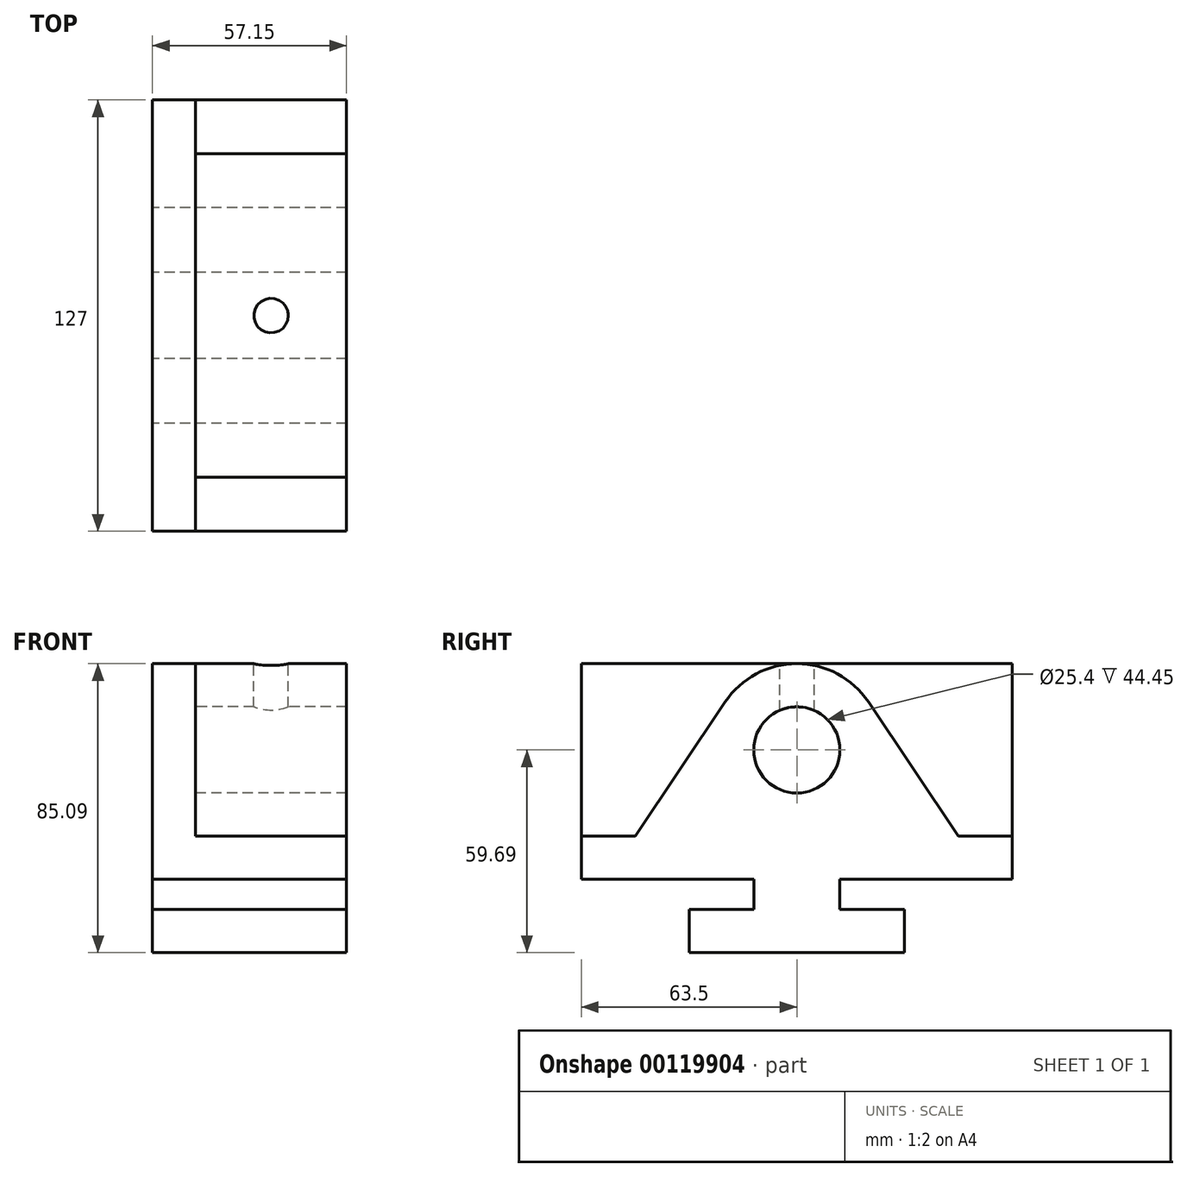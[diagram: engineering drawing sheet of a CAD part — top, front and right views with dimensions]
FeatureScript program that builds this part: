
annotation { "Feature Type Name" : "Feature", "Feature Type Description" : "" }
export const myFeature = defineFeature(function(context is Context, id is Id, definition is map)
    precondition{}
    {
        {
            var Q0;
            Q0=qCreatedBy(makeId("Right.planeOp"),FACE);
            var sketch = newSketch(context, id + "F0", { "sketchPlane" : qUnion([Q0])});
            skLineSegment(sketch, "E0", {"start": v(0, 0) * mm, "end": v(-31.75, 0) * mm});
            skLineSegment(sketch, "E1", {"start": v(-31.75, 0) * mm, "end": v(-31.75, 12.7) * mm});
            skLineSegment(sketch, "E2", {"start": v(-31.75, 12.7) * mm, "end": v(-12.7, 12.7) * mm});
            skLineSegment(sketch, "E3", {"start": v(-12.7, 12.7) * mm, "end": v(-12.7, 21.59) * mm});
            skLineSegment(sketch, "E4", {"start": v(-12.7, 21.59) * mm, "end": v(-63.5, 21.59) * mm});
            skLineSegment(sketch, "E5", {"start": v(-63.5, 21.6) * mm, "end": v(-63.5, 85.1) * mm});
            skLineSegment(sketch, "E6", {"start": v(0, 0) * mm, "end": v(0, 85.09) * mm, "construction": true});
            skLineSegment(sketch, "E7", {"start": v(0, 85.1) * mm, "end": v(-63.5, 85.1) * mm});
            skLineSegment(sketch, "E8.MirrorCS", {"start": v(31.75, 0) * mm, "end": v(31.75, 12.7) * mm});
            skLineSegment(sketch, "E9.MirrorCS", {"start": v(12.7, 21.59) * mm, "end": v(63.5, 21.59) * mm});
            skLineSegment(sketch, "E10.MirrorCS", {"start": v(63.5, 21.6) * mm, "end": v(63.5, 85.1) * mm});
            skLineSegment(sketch, "E11.MirrorCS", {"start": v(31.75, 12.7) * mm, "end": v(12.7, 12.7) * mm});
            skLineSegment(sketch, "E12.MirrorCS", {"start": v(12.7, 12.7) * mm, "end": v(12.7, 21.59) * mm});
            skLineSegment(sketch, "E13", {"start": v(0, 85.1) * mm, "end": v(63.5, 85.1) * mm});
            skLineSegment(sketch, "E14", {"start": v(31.75, 0) * mm, "end": v(0, 0) * mm});
            skLineSegment(sketch, "E15", {"start": v(63.5, 34.3) * mm, "end": v(47.62, 34.3) * mm});
            skLineSegment(sketch, "E16", {"start": v(-63.5, 34.3) * mm, "end": v(-47.63, 34.3) * mm});
            skLineSegment(sketch, "E17", {"start": v(-47.63, 34.29) * mm, "end": v(-21.1, 73.84) * mm});
            skLineSegment(sketch, "E18", {"start": v(47.63, 34.29) * mm, "end": v(21.1, 73.84) * mm});
            skArc(sketch, "E19", {"start": v(21.1, 73.84) * mm, "mid": v(0, 85.09) * mm, "end": v(-21.1, 73.84) * mm});
            skCircle(sketch, "E20", {"center": v(0, 59.69) * mm, "radius": 12.7 * mm});
            skSolve(sketch);
        }
        {
            var Q0;
            Q0=makeQuery(id+"F0.imprint","IMPRINT",FACE,{"disambiguationData":[TD([[makeQuery(id+"F0.imprint","IMPRINT",EDGE,{"derivedFrom":sQuery(id+"F0.wireOp",EDGE,"E0")}),-1.0]])]});
            extrude(context, id + "F1", {"entities" : qUnion([Q0]), "depth" : 44.45 * mm});
        }
        {
            var Q0;
            Q0=makeQuery(id+"F1.opExtrude","CAP_FACE",FACE,{"disambiguationData":[OSD([sQuery(id+"F0.wireOp",EDGE,"E0"),sQuery(id+"F0.wireOp",EDGE,"E1"),sQuery(id+"F0.wireOp",EDGE,"E2"),sQuery(id+"F0.wireOp",EDGE,"E3"),sQuery(id+"F0.wireOp",EDGE,"E4"),sQuery(id+"F0.wireOp",EDGE,"E5"),sQuery(id+"F0.wireOp",EDGE,"E8.MirrorCS"),sQuery(id+"F0.wireOp",EDGE,"E9.MirrorCS"),sQuery(id+"F0.wireOp",EDGE,"E10.MirrorCS"),sQuery(id+"F0.wireOp",EDGE,"E11.MirrorCS"),sQuery(id+"F0.wireOp",EDGE,"E12.MirrorCS"),sQuery(id+"F0.wireOp",EDGE,"E14"),sQuery(id+"F0.wireOp",EDGE,"E15"),sQuery(id+"F0.wireOp",EDGE,"E16"),sQuery(id+"F0.wireOp",EDGE,"E17"),sQuery(id+"F0.wireOp",EDGE,"E18"),sQuery(id+"F0.wireOp",EDGE,"E19"),sQuery(id+"F0.wireOp",EDGE,"E20")])],"isStart":true});
            var sketch = newSketch(context, id + "F2", { "sketchPlane" : qUnion([Q0])});
            skLineSegment(sketch, "E21.bottom", {"start": v(-63.5, 34.3) * mm, "end": v(63.5, 34.3) * mm});
            skLineSegment(sketch, "E21.top", {"start": v(-63.5, 21.6) * mm, "end": v(63.5, 21.6) * mm});
            skLineSegment(sketch, "E21.left", {"start": v(-63.5, 34.3) * mm, "end": v(-63.5, 21.6) * mm});
            skLineSegment(sketch, "E21.right", {"start": v(63.5, 34.3) * mm, "end": v(63.5, 21.6) * mm});
            skSolve(sketch);
        }
        {
            var Q0;
            {var subQ1=sQuery(id+"F0.wireOp",EDGE,"E7");Q0=makeQuery(id+"F0.imprint","IMPRINT",FACE,{"disambiguationData":[TD([[makeQuery(id+"F0.imprint","IMPRINT",EDGE,{"derivedFrom":subQ1}),1.0]])]});}
            var Q1;
            {var subQ2=sQuery(id+"F0.wireOp",EDGE,"E13");Q1=makeQuery(id+"F0.imprint","IMPRINT",FACE,{"disambiguationData":[TD([[makeQuery(id+"F0.imprint","IMPRINT",EDGE,{"derivedFrom":subQ2}),-1.0]])]});}
            var Q2;
            {var subQ5=sQuery(id+"F2.wireOp",EDGE,"E21.left");Q2=makeQuery(id+"F2.imprint","IMPRINT",FACE,{"disambiguationData":[TD([[makeQuery(id+"F2.imprint","IMPRINT",EDGE,{"derivedFrom":subQ5}),-1.0]])]});}
            var Q3;
            Q3=makeQuery(id+"F0.imprint","IMPRINT",FACE,{"disambiguationData":[TD([[makeQuery(id+"F0.imprint","IMPRINT",EDGE,{"derivedFrom":sQuery(id+"F0.wireOp",EDGE,"E20")}),1.0]])]});
            var Q4;
            Q4=makeQuery(id+"F0.imprint","IMPRINT",FACE,{"disambiguationData":[TD([[makeQuery(id+"F0.imprint","IMPRINT",EDGE,{"derivedFrom":sQuery(id+"F0.wireOp",EDGE,"E0")}),-1.0]])]});
            extrude(context, id + "F3", {"entities" : qUnion([Q0, Q1, Q2, Q3, Q4]), "operationType" : NewBodyOperationType.ADD, "oppositeDirection" : true, "depth" : 12.7 * mm});
        }
        {
            var Q0;
            Q0=makeQuery(id+"F3.opExtrude","SWEPT_FACE",FACE,{"disambiguationData":[OSD([sQuery(id+"F0.wireOp",EDGE,"E7"),sQuery(id+"F0.wireOp",EDGE,"E13")])]});
            var sketch = newSketch(context, id + "F4", { "sketchPlane" : qUnion([Q0])});
            skLineSegment(sketch, "E22", {"start": v(0, 0) * mm, "end": v(43.32, 0) * mm, "construction": true});
            skLineSegment(sketch, "E23", {"start": v(22.23, 0) * mm, "end": v(22.22, 42.6) * mm, "construction": true});
            skCircle(sketch, "E24", {"center": v(22.23, 0) * mm, "radius": 5.08 * mm});
            skSolve(sketch);
        }
        {
            var Q0;
            Q0=qSketchRegion(id+"F4",true);
            extrude(context, id + "F5", {"entities" : qUnion([Q0]), "operationType" : NewBodyOperationType.REMOVE, "endBound" : BoundingType.UP_TO_NEXT, "oppositeDirection" : true, "depth" : 25.4 * mm});
        }
    });
